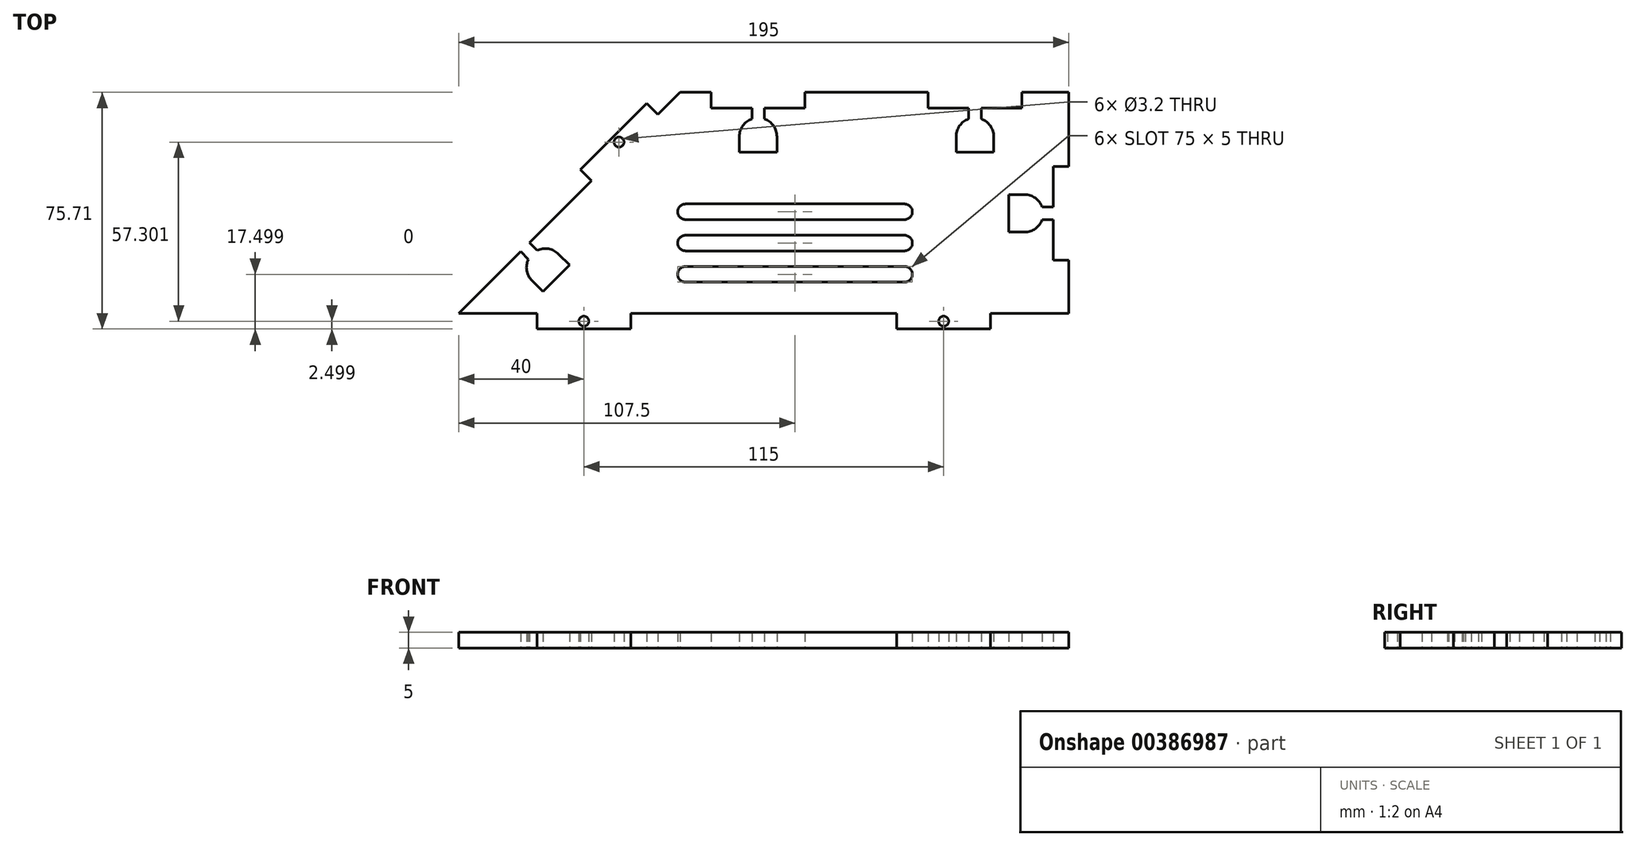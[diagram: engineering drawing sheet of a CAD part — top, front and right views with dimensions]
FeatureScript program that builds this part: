
annotation { "Feature Type Name" : "Feature", "Feature Type Description" : "" }
export const myFeature = defineFeature(function(context is Context, id is Id, definition is map)
    precondition{}
    {
        {
            var Q0;
            Q0=qCreatedBy(makeId("Top.planeOp"),FACE);
            var sketch = newSketch(context, id + "F0", { "sketchPlane" : qUnion([Q0])});
            skLineSegment(sketch, "E0", {"start": v(0, 0) * mm, "end": v(0, -23.71) * mm});
            skLineSegment(sketch, "E1", {"start": v(0, -70.71) * mm, "end": v(-25, -70.71) * mm});
            skLineSegment(sketch, "E2", {"start": v(-195, -70.71) * mm, "end": v(-175.2, -50.91) * mm});
            skLineSegment(sketch, "E3", {"start": v(-124.29, 0) * mm, "end": v(-114.29, 0) * mm});
            skLineSegment(sketch, "E4.top", {"start": v(-25, -75.71) * mm, "end": v(-55, -75.71) * mm});
            skLineSegment(sketch, "E4.left", {"start": v(-25, -70.71) * mm, "end": v(-25, -75.71) * mm});
            skLineSegment(sketch, "E4.right", {"start": v(-55, -70.71) * mm, "end": v(-55, -75.71) * mm});
            skLineSegment(sketch, "E5.top", {"start": v(-170, -75.71) * mm, "end": v(-140, -75.71) * mm});
            skLineSegment(sketch, "E5.left", {"start": v(-170, -70.71) * mm, "end": v(-170, -75.71) * mm});
            skLineSegment(sketch, "E5.right", {"start": v(-140, -70.71) * mm, "end": v(-140, -75.71) * mm});
            skLineSegment(sketch, "E6.trimOffspring", {"start": v(-170, -70.71) * mm, "end": v(-195, -70.71) * mm});
            skLineSegment(sketch, "E7.trimOffspring", {"start": v(-55, -70.71) * mm, "end": v(-140, -70.71) * mm});
            skCircle(sketch, "E8", {"center": v(-155, -73.21) * mm, "radius": 1.6 * mm});
            skCircle(sketch, "E9", {"center": v(-40, -73.21) * mm, "radius": 1.6 * mm});
            skLineSegment(sketch, "E10", {"start": v(-159.53, -55.27) * mm, "end": v(-168.02, -63.75) * mm});
            skLineSegment(sketch, "E11", {"start": v(-159.53, -55.27) * mm, "end": v(-163.07, -51.73) * mm});
            skLineSegment(sketch, "E12", {"start": v(-168.02, -63.75) * mm, "end": v(-171.55, -60.21) * mm});
            skLineSegment(sketch, "E13", {"start": v(-172.37, -48.08) * mm, "end": v(-169.9, -50.56) * mm});
            skLineSegment(sketch, "E14", {"start": v(-175.2, -50.91) * mm, "end": v(-172.73, -53.39) * mm});
            skArc(sketch, "E15", {"start": v(-163.07, -51.73) * mm, "mid": v(-166.3, -50.06) * mm, "end": v(-169.9, -50.56) * mm});
            skArc(sketch, "E16.trimOffspring", {"start": v(-172.73, -53.39) * mm, "mid": v(-173.23, -56.99) * mm, "end": v(-171.55, -60.21) * mm});
            skLineSegment(sketch, "E17.0", {"start": v(-172.73, -53.39) * mm, "end": v(-175.2, -50.91) * mm, "construction": true});
            skLineSegment(sketch, "E18.0", {"start": v(-163.07, -51.73) * mm, "end": v(-171.55, -60.21) * mm, "construction": true});
            skLineSegment(sketch, "E19.trimOffspring", {"start": v(-172.37, -48.08) * mm, "end": v(-152.57, -28.28) * mm});
            skLineSegment(sketch, "E20", {"start": v(-131.36, -7.07) * mm, "end": v(-134.9, -3.54) * mm});
            skLineSegment(sketch, "E21", {"start": v(-134.9, -3.54) * mm, "end": v(-156.1, -24.75) * mm});
            skLineSegment(sketch, "E22", {"start": v(-156.1, -24.75) * mm, "end": v(-152.57, -28.28) * mm});
            skLineSegment(sketch, "E23.trimOffspring", {"start": v(-131.36, -7.07) * mm, "end": v(-124.29, 0) * mm});
            skLineSegment(sketch, "E24", {"start": v(-93.29, -19.16) * mm, "end": v(-105.29, -19.16) * mm});
            skLineSegment(sketch, "E25", {"start": v(-93.29, -19.16) * mm, "end": v(-93.29, -14.16) * mm});
            skLineSegment(sketch, "E26", {"start": v(-105.29, -19.16) * mm, "end": v(-105.29, -14.16) * mm});
            skLineSegment(sketch, "E27", {"start": v(-97.29, -5) * mm, "end": v(-97.29, -8.5) * mm});
            skLineSegment(sketch, "E28", {"start": v(-101.29, -5) * mm, "end": v(-101.29, -8.5) * mm});
            skArc(sketch, "E29", {"start": v(-93.29, -14.16) * mm, "mid": v(-94.4, -10.7) * mm, "end": v(-97.29, -8.5) * mm});
            skArc(sketch, "E30.trimOffspring", {"start": v(-101.29, -8.5) * mm, "mid": v(-104.19, -10.7) * mm, "end": v(-105.29, -14.16) * mm});
            skLineSegment(sketch, "E31.bottom", {"start": v(-84.29, 0) * mm, "end": v(-84.29, -5) * mm});
            skLineSegment(sketch, "E31.top", {"start": v(-114.29, 0) * mm, "end": v(-114.29, -5) * mm});
            skLineSegment(sketch, "E31.right", {"start": v(-84.29, -5) * mm, "end": v(-97.29, -5) * mm});
            skLineSegment(sketch, "E32.trimOffspring", {"start": v(-101.29, -5) * mm, "end": v(-114.29, -5) * mm});
            skLineSegment(sketch, "E33.trimOffspring", {"start": v(-84.29, 0) * mm, "end": v(-45, 0) * mm});
            skLineSegment(sketch, "E34", {"start": v(-24, -19.16) * mm, "end": v(-36, -19.16) * mm});
            skLineSegment(sketch, "E35", {"start": v(-24, -19.16) * mm, "end": v(-24, -14.16) * mm});
            skLineSegment(sketch, "E36", {"start": v(-36, -19.16) * mm, "end": v(-36, -14.16) * mm});
            skLineSegment(sketch, "E37", {"start": v(-28, -5) * mm, "end": v(-28, -8.5) * mm});
            skLineSegment(sketch, "E38", {"start": v(-32, -5) * mm, "end": v(-32, -8.5) * mm});
            skArc(sketch, "E39", {"start": v(-24, -14.16) * mm, "mid": v(-25.1, -10.7) * mm, "end": v(-28, -8.5) * mm});
            skArc(sketch, "E40.trimOffspring", {"start": v(-32, -8.5) * mm, "mid": v(-34.9, -10.7) * mm, "end": v(-36, -14.16) * mm});
            skLineSegment(sketch, "E41.bottom", {"start": v(-15, 0) * mm, "end": v(-15, -5) * mm});
            skLineSegment(sketch, "E41.top", {"start": v(-45, 0) * mm, "end": v(-45, -5) * mm});
            skLineSegment(sketch, "E41.right", {"start": v(-15, -5) * mm, "end": v(-28, -5) * mm});
            skLineSegment(sketch, "E42.trimOffspring", {"start": v(-32, -5) * mm, "end": v(-45, -5) * mm});
            skLineSegment(sketch, "E43.trimOffspring", {"start": v(-15, 0) * mm, "end": v(0, 0) * mm});
            skLineSegment(sketch, "E44", {"start": v(-19.16, -44.71) * mm, "end": v(-19.16, -32.71) * mm});
            skLineSegment(sketch, "E45", {"start": v(-19.16, -44.71) * mm, "end": v(-14.16, -44.71) * mm});
            skLineSegment(sketch, "E46", {"start": v(-19.16, -32.71) * mm, "end": v(-14.16, -32.71) * mm});
            skLineSegment(sketch, "E47", {"start": v(-5, -40.71) * mm, "end": v(-8.5, -40.71) * mm});
            skLineSegment(sketch, "E48", {"start": v(-5, -36.71) * mm, "end": v(-8.5, -36.71) * mm});
            skArc(sketch, "E49", {"start": v(-14.16, -44.71) * mm, "mid": v(-10.7, -43.6) * mm, "end": v(-8.5, -40.71) * mm});
            skArc(sketch, "E50.trimOffspring", {"start": v(-8.5, -36.71) * mm, "mid": v(-10.7, -33.81) * mm, "end": v(-14.16, -32.71) * mm});
            skLineSegment(sketch, "E51.bottom", {"start": v(0, -53.71) * mm, "end": v(-5, -53.71) * mm});
            skLineSegment(sketch, "E51.top", {"start": v(0, -23.71) * mm, "end": v(-5, -23.71) * mm});
            skLineSegment(sketch, "E51.right", {"start": v(-5, -53.71) * mm, "end": v(-5, -40.71) * mm});
            skLineSegment(sketch, "E52.trimOffspring", {"start": v(-5, -36.71) * mm, "end": v(-5, -23.71) * mm});
            skLineSegment(sketch, "E53.trimOffspring", {"start": v(0, -53.71) * mm, "end": v(0, -70.71) * mm});
            skLineSegment(sketch, "E54.bottom", {"start": v(-122.5, -35.71) * mm, "end": v(-52.5, -35.71) * mm});
            skLineSegment(sketch, "E54.top", {"start": v(-122.5, -40.71) * mm, "end": v(-52.5, -40.71) * mm});
            skLineSegment(sketch, "E54.left", {"start": v(-125, -38.21) * mm, "end": v(-125, -38.21) * mm});
            skLineSegment(sketch, "E54.right", {"start": v(-50, -38.21) * mm, "end": v(-50, -38.21) * mm});
            skLineSegment(sketch, "E55.bottom", {"start": v(-122.5, -45.71) * mm, "end": v(-52.5, -45.71) * mm});
            skLineSegment(sketch, "E55.top", {"start": v(-122.5, -50.71) * mm, "end": v(-52.5, -50.71) * mm});
            skLineSegment(sketch, "E55.left", {"start": v(-125, -48.21) * mm, "end": v(-125, -48.21) * mm});
            skLineSegment(sketch, "E55.right", {"start": v(-50, -48.21) * mm, "end": v(-50, -48.21) * mm});
            skLineSegment(sketch, "E56.bottom", {"start": v(-122.5, -55.71) * mm, "end": v(-52.5, -55.71) * mm});
            skLineSegment(sketch, "E56.top", {"start": v(-122.5, -60.71) * mm, "end": v(-52.5, -60.71) * mm});
            skLineSegment(sketch, "E56.left", {"start": v(-125, -58.21) * mm, "end": v(-125, -58.21) * mm});
            skLineSegment(sketch, "E56.right", {"start": v(-50, -58.21) * mm, "end": v(-50, -58.21) * mm});
            skPoint(sketch, "E57.visualSharp", {"position": v(-125, -35.71) * mm});
            skArc(sketch, "E57.filletArc", {"start": v(-122.5, -35.71) * mm, "mid": v(-124.27, -36.44) * mm, "end": v(-125, -38.21) * mm});
            skPoint(sketch, "E58.visualSharp", {"position": v(-125, -40.71) * mm});
            skArc(sketch, "E58.filletArc", {"start": v(-125, -38.21) * mm, "mid": v(-124.27, -39.98) * mm, "end": v(-122.5, -40.71) * mm});
            skPoint(sketch, "E59.visualSharp", {"position": v(-125, -45.71) * mm});
            skArc(sketch, "E59.filletArc", {"start": v(-122.5, -45.71) * mm, "mid": v(-124.27, -46.44) * mm, "end": v(-125, -48.21) * mm});
            skPoint(sketch, "E60.visualSharp", {"position": v(-125, -50.71) * mm});
            skArc(sketch, "E60.filletArc", {"start": v(-125, -48.21) * mm, "mid": v(-124.27, -49.98) * mm, "end": v(-122.5, -50.71) * mm});
            skPoint(sketch, "E61.visualSharp", {"position": v(-125, -55.71) * mm});
            skArc(sketch, "E61.filletArc", {"start": v(-122.5, -55.71) * mm, "mid": v(-124.27, -56.44) * mm, "end": v(-125, -58.21) * mm});
            skPoint(sketch, "E62.visualSharp", {"position": v(-125, -60.71) * mm});
            skArc(sketch, "E62.filletArc", {"start": v(-125, -58.21) * mm, "mid": v(-124.27, -59.98) * mm, "end": v(-122.5, -60.71) * mm});
            skPoint(sketch, "E63.visualSharp", {"position": v(-50, -55.71) * mm});
            skArc(sketch, "E63.filletArc", {"start": v(-50, -58.21) * mm, "mid": v(-50.73, -56.44) * mm, "end": v(-52.5, -55.71) * mm});
            skPoint(sketch, "E64.visualSharp", {"position": v(-50, -60.71) * mm});
            skArc(sketch, "E64.filletArc", {"start": v(-52.5, -60.71) * mm, "mid": v(-50.73, -59.98) * mm, "end": v(-50, -58.21) * mm});
            skPoint(sketch, "E65.visualSharp", {"position": v(-50, -50.71) * mm});
            skArc(sketch, "E65.filletArc", {"start": v(-52.5, -50.71) * mm, "mid": v(-50.73, -49.98) * mm, "end": v(-50, -48.21) * mm});
            skPoint(sketch, "E66.visualSharp", {"position": v(-50, -45.71) * mm});
            skArc(sketch, "E66.filletArc", {"start": v(-50, -48.21) * mm, "mid": v(-50.73, -46.44) * mm, "end": v(-52.5, -45.71) * mm});
            skPoint(sketch, "E67.visualSharp", {"position": v(-50, -35.71) * mm});
            skArc(sketch, "E67.filletArc", {"start": v(-50, -38.21) * mm, "mid": v(-50.73, -36.44) * mm, "end": v(-52.5, -35.71) * mm});
            skPoint(sketch, "E68.visualSharp", {"position": v(-50, -40.71) * mm});
            skArc(sketch, "E68.filletArc", {"start": v(-52.5, -40.71) * mm, "mid": v(-50.73, -39.98) * mm, "end": v(-50, -38.21) * mm});
            skCircle(sketch, "E69", {"center": v(-143.73, -15.9) * mm, "radius": 1.6 * mm});
            skSolve(sketch);
        }
        {
            var Q0;
            Q0=makeQuery(id+"F0.imprint","IMPRINT",FACE,{"disambiguationData":[TD([[makeQuery(id+"F0.imprint","IMPRINT",EDGE,{"derivedFrom":sQuery(id+"F0.wireOp",EDGE,"E0")}),-1.0]])]});
            extrude(context, id + "F1", {"entities" : qUnion([Q0]), "depth" : 5 * mm});
        }
    });
